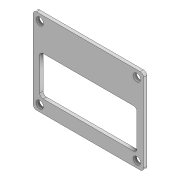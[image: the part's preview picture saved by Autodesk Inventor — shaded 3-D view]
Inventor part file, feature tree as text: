
AUTODESK INVENTOR PART (.ipt)
format: ipt  version: 2020 (Build 240168000, 168)  size: 120,320 bytes
history: native  units: in
note: dims shown in document units (in); Inventor stores cm internally (conversion verified against a paired STEP export)
features: fillet x2, sketch x2, extrude x1, hole x1
ambient origin geometry x8: Origin, YZ Plane, XZ Plane, XY Plane, X Axis, Y Axis, Z Axis, Center Point
bodies: Solid1 (feature_tree)
feature tree (6):
  extrude  "Extrusion1"  Depth=2.0472in
  hole  "Hole1"  [1 undecoded]
  fillet  "Fillet1"  Radius=0.315in
  fillet  "Fillet2"  Radius=0.0787in
  sketch  "Sketch1"  dims[d0=2.65in d1=2.0472in]
  sketch  "Sketch2"  dims[d2=2.335in d4=0.1575in d5=0.315in d6=0.0787in d7=0.0in d8=0.1575in d9=0.1575in d10=0.1575in d11=0.1575in d12=0.1772in d13=0.315in d14=0.375in d15=0.25in d16=0.5635in d17=0.465in d18=0.0in d19=0.7874in d20=0.0787in d21=0.0787in]
note: 1 required parameter value undecoded (feature->parameter linkage not recoverable at this tier; creation-order binding heuristic only, values carry confidence <= 0.55)
